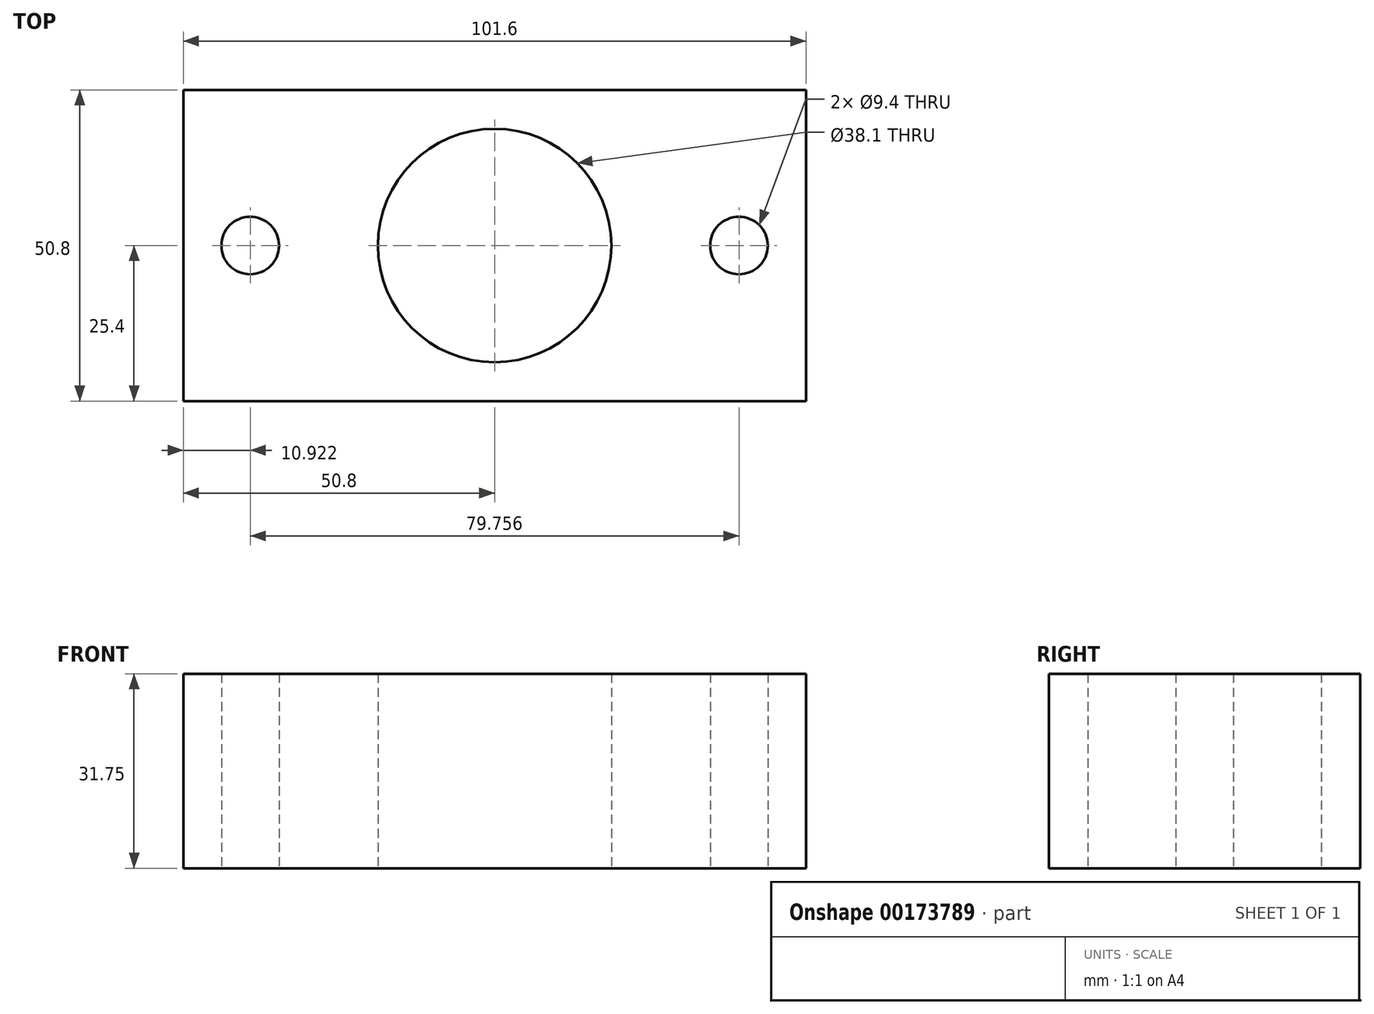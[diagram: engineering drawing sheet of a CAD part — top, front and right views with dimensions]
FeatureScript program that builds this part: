
annotation { "Feature Type Name" : "Feature", "Feature Type Description" : "" }
export const myFeature = defineFeature(function(context is Context, id is Id, definition is map)
    precondition{}
    {
        {
            var Q0;
            Q0=qCreatedBy(makeId("Top.planeOp"),FACE);
            var sketch = newSketch(context, id + "F0", { "sketchPlane" : qUnion([Q0])});
            skLineSegment(sketch, "E0.bottom", {"start": v(50.8, 25.4) * mm, "end": v(-50.8, 25.4) * mm});
            skLineSegment(sketch, "E0.top", {"start": v(50.8, -25.4) * mm, "end": v(-50.8, -25.4) * mm});
            skLineSegment(sketch, "E0.left", {"start": v(50.8, 25.4) * mm, "end": v(50.8, -25.4) * mm});
            skLineSegment(sketch, "E0.right", {"start": v(-50.8, 25.4) * mm, "end": v(-50.8, -25.4) * mm});
            skPoint(sketch, "E0.middle", {"position": v(0, 0) * mm});
            skSolve(sketch);
        }
        {
            var Q0;
            Q0 = qSketchRegion(id + "F0", true);
            extrude(context, id + "F1", {"entities" : qUnion([Q0]), "depth" : 31.75 * mm});
        }
        {
            var Q0;
            Q0=qCreatedBy(makeId("Top.planeOp"),FACE);
            var sketch = newSketch(context, id + "F2", { "sketchPlane" : qUnion([Q0])});
            skCircle(sketch, "E1", {"center": v(0, 0) * mm, "radius": 19.05 * mm});
            skSolve(sketch);
        }
        {
            var Q0;
            Q0 = qSketchRegion(id + "F2", true);
            extrude(context, id + "F3", {"entities" : qUnion([Q0]), "operationType" : NewBodyOperationType.REMOVE, "endBound" : BoundingType.THROUGH_ALL, "depth" : 25.4 * mm});
        }
        {
            var Q0;
            Q0=qCreatedBy(makeId("Top.planeOp"),FACE);
            var sketch = newSketch(context, id + "F4", { "sketchPlane" : qUnion([Q0])});
            skCircle(sketch, "E2", {"center": v(-39.88, 0) * mm, "radius": 4.7 * mm});
            skCircle(sketch, "E3", {"center": v(39.88, 0) * mm, "radius": 4.7 * mm});
            skSolve(sketch);
        }
        {
            var Q0;
            Q0 = qSketchRegion(id + "F4", true);
            extrude(context, id + "F5", {"entities" : qUnion([Q0]), "operationType" : NewBodyOperationType.REMOVE, "endBound" : BoundingType.THROUGH_ALL, "depth" : 25.4 * mm});
        }
    });
